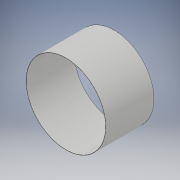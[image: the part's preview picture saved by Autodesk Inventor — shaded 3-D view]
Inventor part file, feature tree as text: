
AUTODESK INVENTOR PART (.ipt)
format: ipt  version: 2019 (Build 230136000, 136)  size: 103,936 bytes
history: native  units: mm
features: extrude x2, sketch x2
ambient origin geometry x8: Origin, YZ Plane, XZ Plane, XY Plane, X Axis, Y Axis, Z Axis, Center Point
bodies: Solid1 (feature_tree)
feature tree (4):
  extrude  "Extrusion1"  Depth=120.6mm TaperAngle=0.0deg
  extrude  "Extrusion2"  Depth=12.06mm TaperAngle=0.0deg
  sketch  "Sketch1"  dims[d0=199.7mm d1=120.6mm d2=0.0mm]
  sketch  "Sketch2"  dims[d3=198.7mm d4=12.06mm d5=0.0mm]
